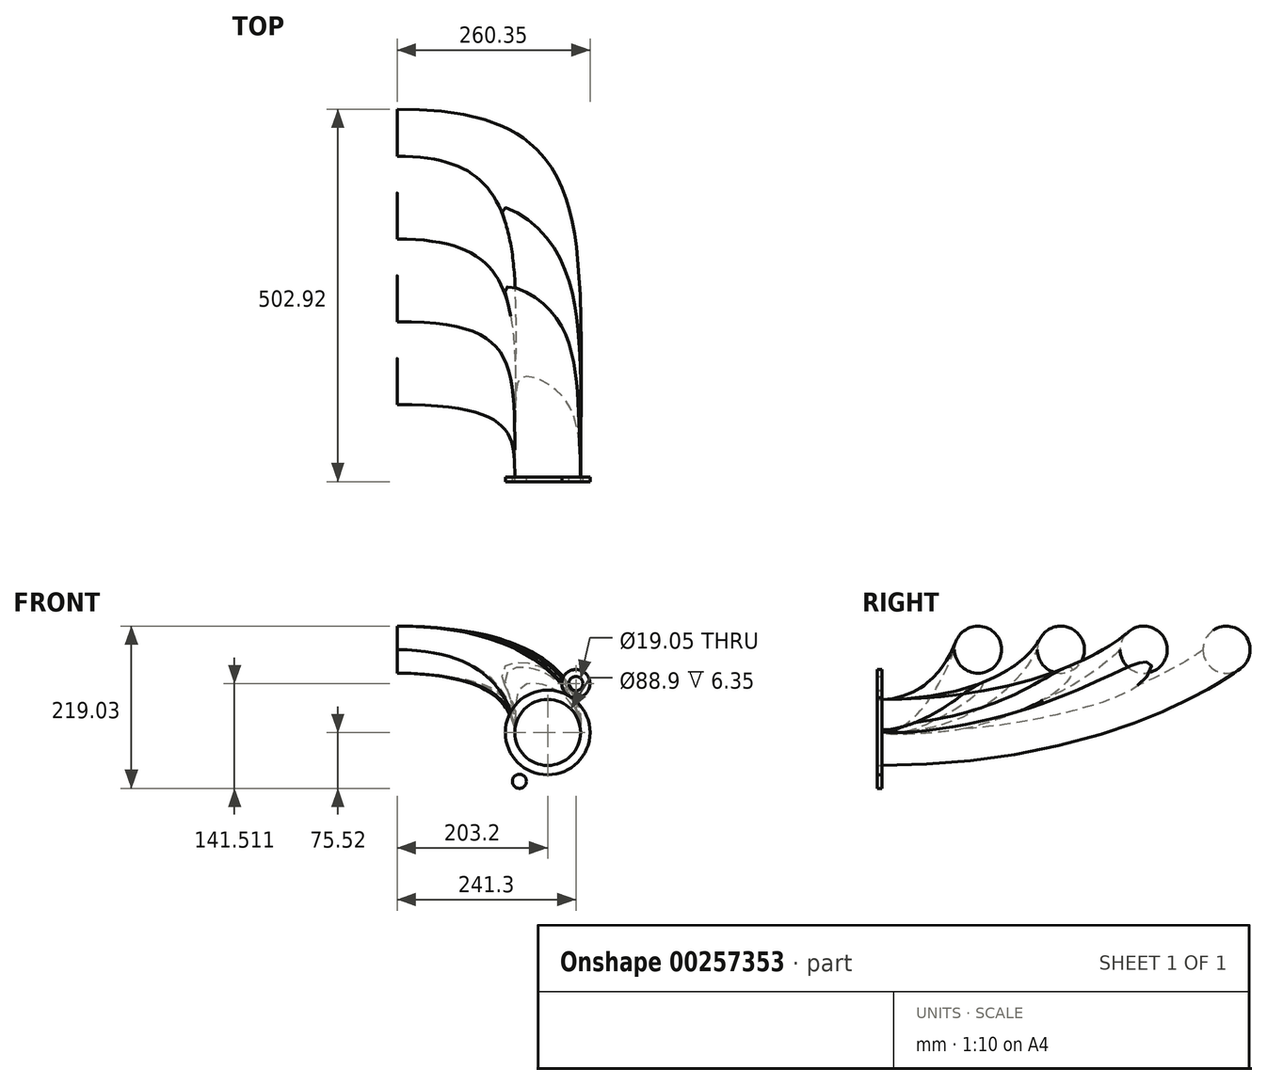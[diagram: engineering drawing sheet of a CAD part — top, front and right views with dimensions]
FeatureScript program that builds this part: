
annotation { "Feature Type Name" : "Feature", "Feature Type Description" : "" }
export const myFeature = defineFeature(function(context is Context, id is Id, definition is map)
    precondition{}
    {
        {
            var Q0;
            Q0=qCreatedBy(makeId("Right.planeOp"),FACE);
            cPlane(context, id + "F0", {"entities" : qUnion([Q0]), "cplaneType" : CPlaneType.OFFSET, "offset" : 203.2 * mm, "oppositeDirection" : true, "width" : 152.4 * mm, "height" : 152.4 * mm});
        }
        {
            var Q0;
            Q0=qCreatedBy(makeId("Top.planeOp"),FACE);
            cPlane(context, id + "F1", {"entities" : qUnion([Q0]), "cplaneType" : CPlaneType.OFFSET, "offset" : 111.76 * mm, "width" : 152.4 * mm, "height" : 152.4 * mm});
        }
        {
            var Q0;
            Q0=qCreatedBy(makeId("Front.planeOp"),FACE);
            var sketch = newSketch(context, id + "F2", { "sketchPlane" : qUnion([Q0])});
            skCircle(sketch, "E0", {"center": v(0, 0) * mm, "radius": 44.45 * mm});
            skSolve(sketch);
        }
        {
            var Q0;
            Q0=qCreatedBy(id+"F0.planeOp",FACE);
            var sketch = newSketch(context, id + "F3", { "sketchPlane" : qUnion([Q0])});
            skCircle(sketch, "E1", {"center": v(129.54, 111.76) * mm, "radius": 31.75 * mm});
            skCircle(sketch, "E2.1.0.0", {"center": v(241.3, 111.76) * mm, "radius": 31.75 * mm});
            skCircle(sketch, "E2.2.0.0", {"center": v(353.06, 111.76) * mm, "radius": 31.75 * mm});
            skCircle(sketch, "E2.3.0.0", {"center": v(464.82, 111.76) * mm, "radius": 31.75 * mm});
            skLineSegment(sketch, "E2.direction1", {"start": v(129.54, 111.76) * mm, "end": v(241.3, 111.76) * mm, "construction": true});
            skSolve(sketch);
        }
        {
            var Q0;
            Q0=qCreatedBy(id+"F1.planeOp",FACE);
            var sketch = newSketch(context, id + "F4", { "sketchPlane" : qUnion([Q0])});
            skLineSegment(sketch, "E3.0", {"start": v(-203.2, 129.54) * mm, "end": v(-203.2, 161.3) * mm});
            skLineSegment(sketch, "E4.0", {"start": v(-203.2, 161.3) * mm, "end": v(-203.2, 97.8) * mm});
            skLineSegment(sketch, "E5.0", {"start": v(-203.2, 273.05) * mm, "end": v(-203.2, 209.55) * mm});
            skLineSegment(sketch, "E6.0", {"start": v(-203.2, 384.81) * mm, "end": v(-203.2, 321.31) * mm});
            skLineSegment(sketch, "E7.0", {"start": v(-203.2, 496.57) * mm, "end": v(-203.2, 433.07) * mm});
            skLineSegment(sketch, "E8.trimOffspring", {"start": v(-203.2, 209.55) * mm, "end": v(-203.2, 241.3) * mm});
            skLineSegment(sketch, "E9", {"start": v(-203.2, 97.8) * mm, "end": v(-177.8, 97.8) * mm});
            skLineSegment(sketch, "E10.0.1.0", {"start": v(-203.2, 209.55) * mm, "end": v(-177.8, 209.55) * mm});
            skLineSegment(sketch, "E10.0.2.0", {"start": v(-203.2, 321.31) * mm, "end": v(-177.8, 321.31) * mm});
            skLineSegment(sketch, "E10.0.3.0", {"start": v(-203.2, 433.07) * mm, "end": v(-177.8, 433.07) * mm});
            skLineSegment(sketch, "E10.direction1", {"start": v(-203.2, 97.8) * mm, "end": v(-177.8, 97.8) * mm, "construction": true});
            skLineSegment(sketch, "E10.direction2", {"start": v(-203.2, 97.8) * mm, "end": v(-203.2, 209.55) * mm, "construction": true});
            skSolve(sketch);
        }
        {
            var Q0;
            Q0=qCreatedBy(makeId("Top.planeOp"),FACE);
            var sketch = newSketch(context, id + "F5", { "sketchPlane" : qUnion([Q0])});
            skLineSegment(sketch, "E11.0", {"start": v(44.45, 0) * mm, "end": v(-44.45, 0) * mm});
            skLineSegment(sketch, "E12", {"start": v(-44.45, 0) * mm, "end": v(-44.45, 25.4) * mm});
            skSolve(sketch);
        }
        {
            var Q0;
            Q0=makeQuery(id+"F2.imprint","IMPRINT",FACE,{"disambiguationData":[TD([[makeQuery(id+"F2.imprint","IMPRINT",EDGE,{"derivedFrom":sQuery(id+"F2.wireOp",EDGE,"E0")}),1.0]])]});
            var Q1;
            Q1=makeQuery(id+"F3.imprint","IMPRINT",FACE,{"disambiguationData":[TD([[makeQuery(id+"F3.imprint","IMPRINT",EDGE,{"derivedFrom":sQuery(id+"F3.wireOp",EDGE,"E1")}),1.0]])]});
            var Q2;
            Q2=sQuery(id+"F4.wireOp",VERTEX,"E4.0.end");
            var Q3;
            Q3=sQuery(id+"F5.wireOp",VERTEX,"E12.start");
            loft(context, id + "F6", {"startCondition" : LoftEndDerivativeType.NORMAL_TO_PROFILE, "startMagnitude" : 1.6, "endCondition" : LoftEndDerivativeType.NORMAL_TO_PROFILE, "endMagnitude" : 2.9, "sheetProfilesArray" : [{ "sheetProfileEntities" : qUnion([Q0]) }, { "sheetProfileEntities" : qUnion([Q1]) }], "matchConnections" : true, "connections" : [{ "connectionEntities" : qUnion([Q2, Q3]), "connectionEdgeQueries" : qUnion([]), "connectionEdgeParameters" : [] }]});
        }
        {
            var Q1;
            Q1=makeQuery(id+"F2.imprint","IMPRINT",FACE,{"disambiguationData":[TD([[makeQuery(id+"F2.imprint","IMPRINT",EDGE,{"derivedFrom":sQuery(id+"F2.wireOp",EDGE,"E0")}),1.0]])]});
            var Q2;
            Q2=makeQuery(id+"F3.imprint","IMPRINT",FACE,{"disambiguationData":[TD([[makeQuery(id+"F3.imprint","IMPRINT",EDGE,{"derivedFrom":sQuery(id+"F3.wireOp",EDGE,"E2.1.0.0")}),1.0]])]});
            var Q3;
            Q3=sQuery(id+"F4.wireOp",VERTEX,"E8.trimOffspring.start");
            var Q4;
            Q4=sQuery(id+"F5.wireOp",VERTEX,"E12.start");
            loft(context, id + "F7", {"operationType" : NewBodyOperationType.ADD, "startCondition" : LoftEndDerivativeType.NORMAL_TO_PROFILE, "startMagnitude" : 2.2, "endCondition" : LoftEndDerivativeType.NORMAL_TO_PROFILE, "endMagnitude" : 2.9, "sheetProfilesArray" : [{ "sheetProfileEntities" : qUnion([Q1]) }, { "sheetProfileEntities" : qUnion([Q2]) }], "matchConnections" : true, "connections" : [{ "connectionEntities" : qUnion([Q3, Q4]), "connectionEdgeQueries" : qUnion([]), "connectionEdgeParameters" : [] }]});
        }
        {
            var Q1;
            Q1=makeQuery(id+"F3.imprint","IMPRINT",FACE,{"disambiguationData":[TD([[makeQuery(id+"F3.imprint","IMPRINT",EDGE,{"derivedFrom":sQuery(id+"F3.wireOp",EDGE,"E2.2.0.0")}),1.0]])]});
            var Q2;
            Q2=makeQuery(id+"F2.imprint","IMPRINT",FACE,{"disambiguationData":[TD([[makeQuery(id+"F2.imprint","IMPRINT",EDGE,{"derivedFrom":sQuery(id+"F2.wireOp",EDGE,"E0")}),1.0]])]});
            var Q3;
            Q3=sQuery(id+"F4.wireOp",VERTEX,"E6.0.end");
            var Q4;
            Q4=sQuery(id+"F5.wireOp",VERTEX,"E12.start");
            loft(context, id + "F8", {"operationType" : NewBodyOperationType.ADD, "startCondition" : LoftEndDerivativeType.NORMAL_TO_PROFILE, "startMagnitude" : 3, "endCondition" : LoftEndDerivativeType.NORMAL_TO_PROFILE, "endMagnitude" : 2, "sheetProfilesArray" : [{ "sheetProfileEntities" : qUnion([Q1]) }, { "sheetProfileEntities" : qUnion([Q2]) }], "matchConnections" : true, "connections" : [{ "connectionEntities" : qUnion([Q3, Q4]), "connectionEdgeQueries" : qUnion([]), "connectionEdgeParameters" : [] }]});
        }
        {
            var Q1;
            Q1=makeQuery(id+"F3.imprint","IMPRINT",FACE,{"disambiguationData":[TD([[makeQuery(id+"F3.imprint","IMPRINT",EDGE,{"derivedFrom":sQuery(id+"F3.wireOp",EDGE,"E2.3.0.0")}),1.0]])]});
            var Q2;
            Q2=makeQuery(id+"F2.imprint","IMPRINT",FACE,{"disambiguationData":[TD([[makeQuery(id+"F2.imprint","IMPRINT",EDGE,{"derivedFrom":sQuery(id+"F2.wireOp",EDGE,"E0")}),1.0]])]});
            var Q3;
            Q3=sQuery(id+"F4.wireOp",VERTEX,"E10.0.3.0.start");
            var Q4;
            Q4=sQuery(id+"F5.wireOp",VERTEX,"E12.start");
            loft(context, id + "F9", {"operationType" : NewBodyOperationType.ADD, "startCondition" : LoftEndDerivativeType.NORMAL_TO_PROFILE, "startMagnitude" : 3, "endCondition" : LoftEndDerivativeType.NORMAL_TO_PROFILE, "endMagnitude" : 2, "sheetProfilesArray" : [{ "sheetProfileEntities" : qUnion([Q1]) }, { "sheetProfileEntities" : qUnion([Q2]) }], "matchConnections" : true, "connections" : [{ "connectionEntities" : qUnion([Q3, Q4]), "connectionEdgeQueries" : qUnion([]), "connectionEdgeParameters" : [] }]});
        }
        {
            var Q0;
            Q0=makeQuery(id+"F2.imprint","IMPRINT",FACE,{"disambiguationData":[TD([[makeQuery(id+"F2.imprint","IMPRINT",EDGE,{"derivedFrom":sQuery(id+"F2.wireOp",EDGE,"E0")}),1.0]])]});
            var sketch = newSketch(context, id + "F10", { "sketchPlane" : qUnion([Q0])});
            skCircle(sketch, "E13", {"center": v(0, 0) * mm, "radius": 57.15 * mm});
            skCircle(sketch, "E14", {"center": v(0, 0) * mm, "radius": 38.1 * mm});
            skCircle(sketch, "E15", {"center": v(38.1, 66) * mm, "radius": 19.05 * mm});
            skCircle(sketch, "E16", {"center": v(52.39, 41.24) * mm, "radius": 9.53 * mm});
            skCircle(sketch, "E17", {"center": v(9.53, 66) * mm, "radius": 9.53 * mm});
            skCircle(sketch, "E18", {"center": v(38.1, 66) * mm, "radius": 9.53 * mm});
            skLineSegment(sketch, "E19", {"start": v(0, 0) * mm, "end": v(38.1, 66) * mm, "construction": true});
            skLineSegment(sketch, "E20", {"start": v(0, 0) * mm, "end": v(-158.26, 91.37) * mm, "construction": true});
            skCircle(sketch, "E21.MirrorC", {"center": v(-52.39, -41.24) * mm, "radius": 9.53 * mm});
            skCircle(sketch, "E22.MirrorC", {"center": v(-38.1, -66) * mm, "radius": 19.05 * mm});
            skCircle(sketch, "E23.MirrorC", {"center": v(-38.1, -66) * mm, "radius": 9.53 * mm});
            skCircle(sketch, "E24.MirrorC", {"center": v(-9.52, -66) * mm, "radius": 9.53 * mm});
            skSolve(sketch);
        }
        {
            var Q0;
            Q0=makeQuery(id+"F10.imprint","IMPRINT",FACE,{"disambiguationData":[TD([[makeQuery(id+"F10.imprint","IMPRINT",EDGE,{"derivedFrom":makeQuery(id+"F2.imprint","IMPRINT",EDGE,{"derivedFrom":sQuery(id+"F2.wireOp",EDGE,"E0")})}),-1.0]])]});
            var Q1;
            Q1=makeQuery(id+"F10.imprint","IMPRINT",FACE,{"disambiguationData":[TD([[makeQuery(id+"F10.imprint","IMPRINT",EDGE,{"derivedFrom":sQuery(id+"F10.wireOp",EDGE,"E18")}),-1.0]])]});
            var Q2;
            Q2=makeQuery(id+"F10.imprint","IMPRINT",FACE,{"disambiguationData":[TD([[makeQuery(id+"F10.imprint","IMPRINT",EDGE,{"derivedFrom":sQuery(id+"F10.wireOp",EDGE,"E23.MirrorC")}),1.0]])]});
            extrude(context, id + "F11", {"entities" : qUnion([Q0, Q1, Q2]), "depth" : 6.35 * mm});
        }
    });
